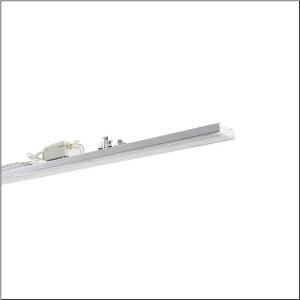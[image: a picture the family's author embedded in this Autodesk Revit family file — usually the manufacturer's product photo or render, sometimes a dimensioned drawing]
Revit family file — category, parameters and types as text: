
# Revit family: licross_r__21_recessed_mo_52tl11dn455g_e53e
name_source: partatom
category: Lighting Fixtures
units: mm (PartAtom-declared; Revit-internal decimal feet)

## family parameters
Cut with Voids When Loaded = No
Host = Face
Light Source = No
Part Type = Normal
Room Calculation Point = No
Round Connector Dimension = Use Diameter
Shared = No

## types (1)
- --- (1 x LED, 5800 lm, 31.8 W, 4000K)
    Apparent Load = 32 VA
    CIE Flux Codes = 89 96 99 100 100
    Color Rendering = 80
    Color Temperature = 4000K
    Default Elevation = 1800 mm
    Description = Licross® 21 Recessed MO, luminaire insert, of sheet steel, galvanised, coil coated, white, length: 1.500mm, width: 66mm, height: 67mm, LED rated luminous flux: 5.800lm, light colour: 840, control gear: DALI 2, with plug, 5-pole, with phase selection, mains connection: 220..240V, AC, 50/60Hz, rated input power: 32W, halogen-free wiring, primary light control with lens, of plastic, primary optical cover: cover, of PMMA, light emission: direct distribution, primary light characteristic: symmetric, protection rating (complete): IP40, insulation class (complete): insulation class I (protective earthing), certification: CE, ENEC, VDE, UKCA, protection symbol: D if used in an environment without relevant dust loads with corresponding accessories, impact resistance: IK06, permissible ambient temperature for indoor applications: -25..+45°C, corresponds to IFS (International Featured Standards) requirements for safety and quality in the food industry, reducing of maximum allowable ambient temperature of 5°C with ceiling mounting, LABS conformity tested according to VDMA 24364:2018-05, packaging unit: 1 piece
    Height = 58 mm
    Lamp = 1 x LED
    Lamp Light Flux = 5800 lm
    Lamp Power = 31.8 W
    Lamp count = 1
    Length = 1500 mm
    Luminous efficacy = 182 lm/W
    Manufacturer = Siteco
    ModVariant = No
    Model = 52TL11DN455G
    Mounting Place = Ceiling
    Mounting Type = Pendant
    Number of Poles = 1
    OnlyDefault = Yes
    Power Factor = 1
    Product Name = Licross® 21 Recessed MO
    Product group = luminaire insert
    ProductGroupID = 901
    Protection Class = Protection class I
    Protection Degree = IP 40
    RLX_Detail_Level = 1
    RLX_Emergency_Light_Flux = 0 lm
    RLX_Emergency_Type = 0
    RLX_Emergency_Type_DB = No
    RlxData = <blob elided: 24133 chars, md5=9186d1f1>
    Socket = socket
    Standby Power = 0 W
    System Light Flux = 5800 lm
    System Power = 32 W
    Type Comments = factory setting: luminous flux: 100 % | dim-lin: 254 | 215 mA
    Type Image = l_1296930.jpg
    URL = http://relux.com
    VarID = @adj_058501
    Voltage = 0 V
    Weight = 0.00 kg
    Width = 66 mm

## geometry (parser evidence)
native form markers: Blend x4, Sweep x11
no freeform markers — native parametric forms only
